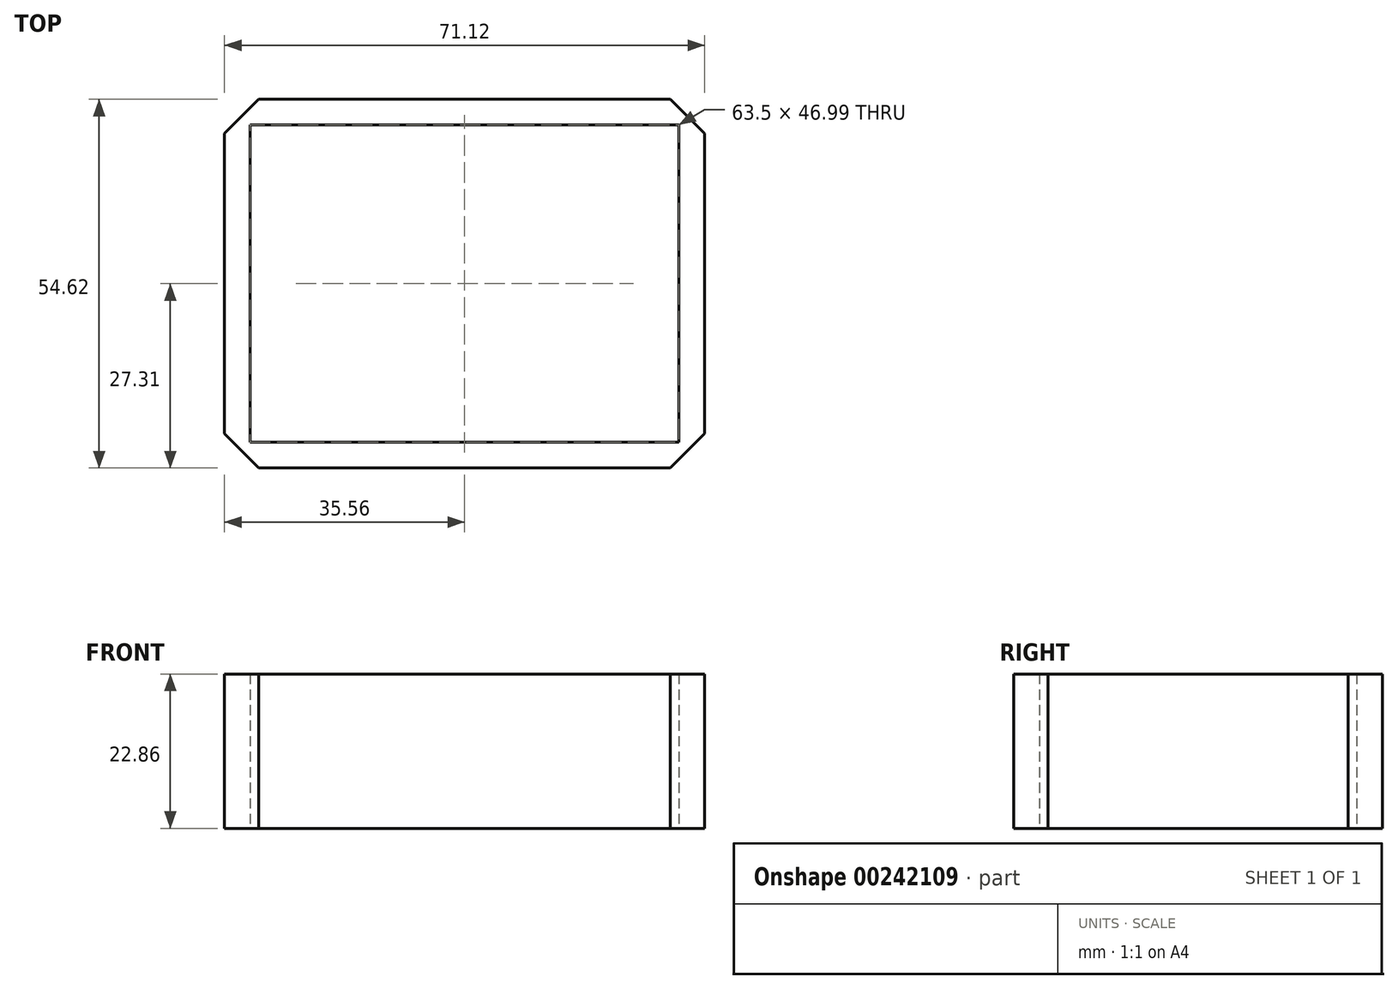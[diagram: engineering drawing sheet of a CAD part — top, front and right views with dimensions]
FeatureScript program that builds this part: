
annotation { "Feature Type Name" : "Feature", "Feature Type Description" : "" }
export const myFeature = defineFeature(function(context is Context, id is Id, definition is map)
    precondition{}
    {
        {
            var Q0;
            Q0=qCreatedBy(makeId("Top.planeOp"),FACE);
            var sketch = newSketch(context, id + "F0", { "sketchPlane" : qUnion([Q0])});
            skLineSegment(sketch, "E0.bottom", {"start": v(-31.75, 23.5) * mm, "end": v(31.75, 23.5) * mm});
            skLineSegment(sketch, "E0.top", {"start": v(-31.75, -23.5) * mm, "end": v(31.75, -23.5) * mm});
            skLineSegment(sketch, "E0.left", {"start": v(-31.75, 23.5) * mm, "end": v(-31.75, -23.5) * mm});
            skLineSegment(sketch, "E0.right", {"start": v(31.75, 23.5) * mm, "end": v(31.75, -23.5) * mm});
            skPoint(sketch, "E0.middle", {"position": v(0, 0) * mm});
            skLineSegment(sketch, "E1.0", {"start": v(-35.56, 27.3) * mm, "end": v(35.56, 27.3) * mm});
            skLineSegment(sketch, "E1.1", {"start": v(-35.56, 27.3) * mm, "end": v(-35.56, -27.3) * mm});
            skLineSegment(sketch, "E1.2", {"start": v(-35.56, -27.3) * mm, "end": v(35.56, -27.3) * mm});
            skLineSegment(sketch, "E1.3", {"start": v(35.56, 27.3) * mm, "end": v(35.56, -27.3) * mm});
            skSolve(sketch);
        }
        {
            var Q0;
            Q0 = qSketchRegion(id + "F0", true);
            extrude(context, id + "F1", {"entities" : qUnion([Q0]), "depth" : 22.86 * mm});
        }
        {
            var Q0;
            Q0=makeQuery(id+"F1.opExtrude","SWEPT_EDGE",EDGE,{"disambiguationData":[OSD([sQuery(id+"F0.wireOp",EDGE,"E1.2"),sQuery(id+"F0.wireOp",EDGE,"E1.3")])]});
            var Q1;
            Q1=makeQuery(id+"F1.opExtrude","SWEPT_EDGE",EDGE,{"disambiguationData":[OSD([sQuery(id+"F0.wireOp",EDGE,"E1.0"),sQuery(id+"F0.wireOp",EDGE,"E1.1")])]});
            var Q2;
            Q2=makeQuery(id+"F1.opExtrude","SWEPT_EDGE",EDGE,{"disambiguationData":[OSD([sQuery(id+"F0.wireOp",EDGE,"E1.0"),sQuery(id+"F0.wireOp",EDGE,"E1.3")])]});
            var Q3;
            Q3=makeQuery(id+"F1.opExtrude","SWEPT_EDGE",EDGE,{"disambiguationData":[OSD([sQuery(id+"F0.wireOp",EDGE,"E1.1"),sQuery(id+"F0.wireOp",EDGE,"E1.2")])]});
            chamfer(context, id + "F2", {"entities" : qUnion([Q0, Q1, Q2, Q3]), "width" : 5.08 * mm, "tangentPropagation" : true});
        }
    });
